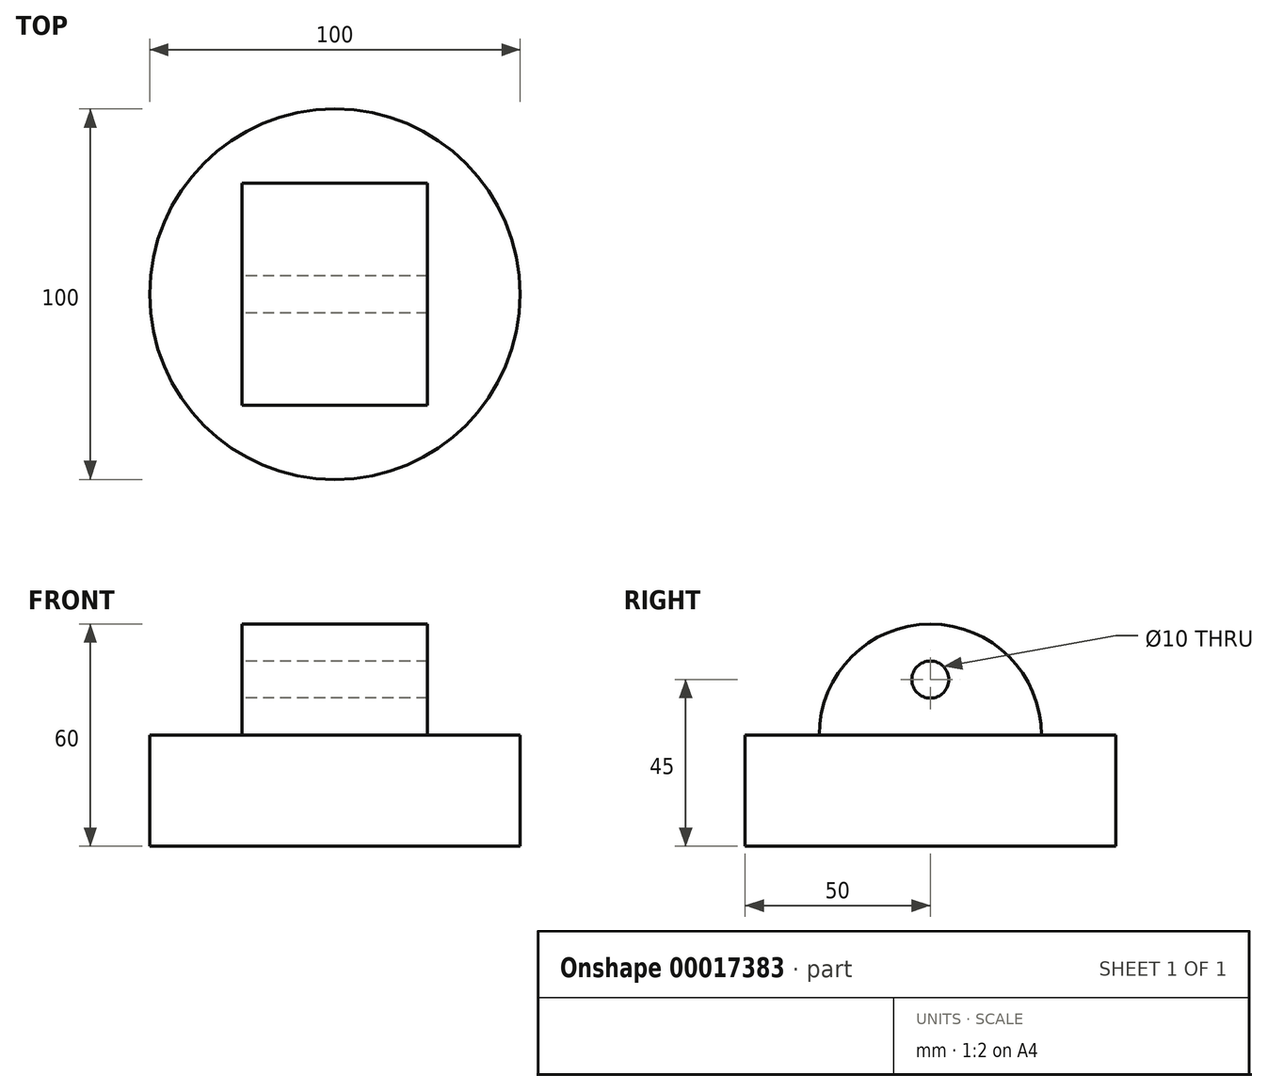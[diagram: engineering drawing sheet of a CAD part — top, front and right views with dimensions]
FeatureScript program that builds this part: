
annotation { "Feature Type Name" : "Feature", "Feature Type Description" : "" }
export const myFeature = defineFeature(function(context is Context, id is Id, definition is map)
    precondition{}
    {
        {
            var Q0;
            Q0=qCreatedBy(makeId("Top.planeOp"),FACE);
            var sketch = newSketch(context, id + "F0", { "sketchPlane" : qUnion([Q0])});
            skCircle(sketch, "E0", {"center": v(0, 0) * mm, "radius": 50 * mm});
            skLineSegment(sketch, "E1", {"start": v(0, 0) * mm, "end": v(0, 50) * mm});
            skSolve(sketch);
        }
        {
            var Q0;
            Q0=qSketchRegion(id+"F0",true);
            extrude(context, id + "F1", {"entities" : qUnion([Q0]), "depth" : 30 * mm});
        }
        {
            var Q0;
            Q0=qCreatedBy(makeId("Right.planeOp"),FACE);
            var sketch = newSketch(context, id + "F2", { "sketchPlane" : qUnion([Q0])});
            skCircle(sketch, "E2", {"center": v(0, 30) * mm, "radius": 30 * mm});
            skLineSegment(sketch, "E3", {"start": v(0, 30) * mm, "end": v(-30, 30) * mm});
            skLineSegment(sketch, "E4", {"start": v(0, 30) * mm, "end": v(0, 45) * mm});
            skCircle(sketch, "E5", {"center": v(0, 45) * mm, "radius": 5 * mm});
            skLineSegment(sketch, "E6", {"start": v(0, 45) * mm, "end": v(5, 45) * mm});
            skSolve(sketch);
        }
        {
            var Q0;
            Q0=qSketchRegion(id+"F2",true);
            extrude(context, id + "F3", {"entities" : qUnion([Q0]), "operationType" : NewBodyOperationType.ADD, "depth" : 25 * mm, "hasSecondDirection" : true, "secondDirectionOppositeDirection" : true, "secondDirectionDepth" : 25 * mm});
        }
    });
